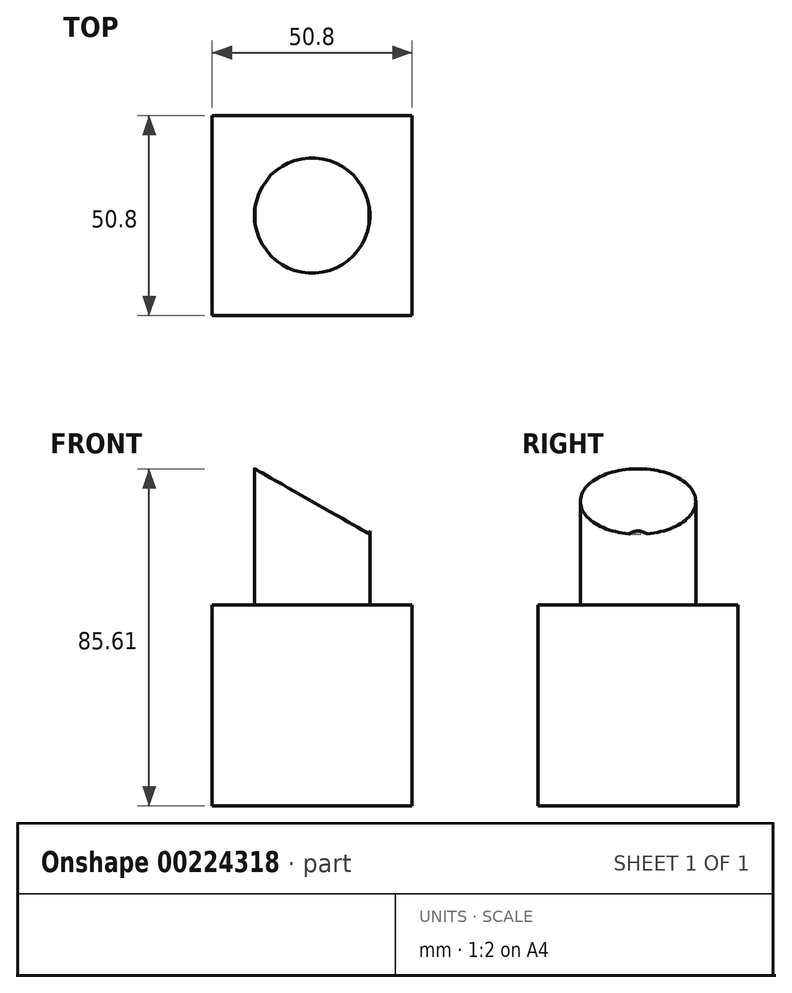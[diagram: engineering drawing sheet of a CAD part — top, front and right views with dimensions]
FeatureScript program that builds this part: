
annotation { "Feature Type Name" : "Feature", "Feature Type Description" : "" }
export const myFeature = defineFeature(function(context is Context, id is Id, definition is map)
    precondition{}
    {
        {
            var Q0;
            Q0=qCreatedBy(makeId("Top.planeOp"),FACE);
            var sketch = newSketch(context, id + "F0", { "sketchPlane" : qUnion([Q0])});
            skLineSegment(sketch, "E0.bottom", {"start": v(25.4, 25.4) * mm, "end": v(-25.4, 25.4) * mm});
            skLineSegment(sketch, "E0.top", {"start": v(25.4, -25.4) * mm, "end": v(-25.4, -25.4) * mm});
            skLineSegment(sketch, "E0.right", {"start": v(-25.4, 25.4) * mm, "end": v(-25.4, -25.4) * mm});
            skPoint(sketch, "E0.middle", {"position": v(0, 0) * mm});
            skLineSegment(sketch, "E1", {"start": v(25.4, 25.4) * mm, "end": v(25.4, -25.4) * mm});
            skSolve(sketch);
        }
        {
            var Q0;
            Q0 = qSketchRegion(id + "F0", true);
            extrude(context, id + "F1", {"entities" : qUnion([Q0]), "depth" : 51.05 * mm});
        }
        {
            var Q0;
            Q0=makeQuery(id+"F1.opExtrude","CAP_FACE",FACE,{"disambiguationData":[OSD([sQuery(id+"F0.wireOp",EDGE,"E0.bottom"),sQuery(id+"F0.wireOp",EDGE,"E0.top"),sQuery(id+"F0.wireOp",EDGE,"E0.left"),sQuery(id+"F0.wireOp",EDGE,"E0.right")])],"isStart":false});
            var sketch = newSketch(context, id + "F2", { "sketchPlane" : qUnion([Q0])});
            skCircle(sketch, "E2", {"center": v(0, 0) * mm, "radius": 14.68 * mm});
            skSolve(sketch);
        }
        {
            var Q0;
            Q0 = qSketchRegion(id + "F2", true);
            extrude(context, id + "F3", {"entities" : qUnion([Q0]), "operationType" : NewBodyOperationType.ADD, "depth" : 43.69 * mm});
        }
        {
            var Q0;
            Q0=qCreatedBy(makeId("Front.planeOp"),FACE);
            var sketch = newSketch(context, id + "F4", { "sketchPlane" : qUnion([Q0])});
            skLineSegment(sketch, "E3", {"start": v(-14.5, 85.61) * mm, "end": v(14.5, 69.14) * mm});
            skLineSegment(sketch, "E4", {"start": v(14.5, 69.14) * mm, "end": v(21.1, 95.28) * mm});
            skLineSegment(sketch, "E5", {"start": v(21.1, 95.28) * mm, "end": v(-17.36, 97.04) * mm});
            skLineSegment(sketch, "E6", {"start": v(-17.36, 97.04) * mm, "end": v(-17.88, 85.61) * mm});
            skLineSegment(sketch, "E7", {"start": v(-17.88, 85.61) * mm, "end": v(-14.5, 85.61) * mm});
            skSolve(sketch);
        }
        {
            var Q0;
            Q0=makeQuery(id+"F4.imprint","IMPRINT",FACE,{"disambiguationData":[TD([[makeQuery(id+"F4.imprint","IMPRINT",EDGE,{"derivedFrom":sQuery(id+"F4.wireOp",EDGE,"E3")}),1.0]])]});
            extrude(context, id + "F5", {"entities" : qUnion([Q0]), "operationType" : NewBodyOperationType.REMOVE, "depth" : 25.4 * mm});
        }
        {
            var Q0;
            Q0 = qSketchRegion(id + "F4", true);
            extrude(context, id + "F6", {"entities" : qUnion([Q0]), "operationType" : NewBodyOperationType.REMOVE, "oppositeDirection" : true, "depth" : 25.4 * mm});
        }
    });
